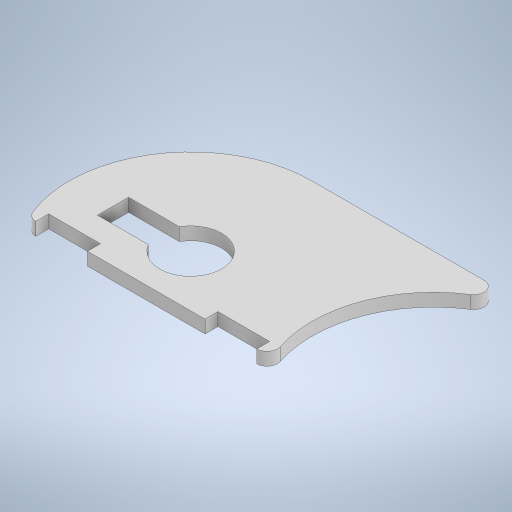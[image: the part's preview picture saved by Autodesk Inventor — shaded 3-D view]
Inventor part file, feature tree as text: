
AUTODESK INVENTOR PART (.ipt)
format: ipt  version: 2024.1 (Build 281209000, 209)  size: 267,264 bytes
history: native  units: mm
features: extrude x2, sketch x2, other x1, fillet x1
ambient origin geometry x8: Origin, YZ Plane, XZ Plane, XY Plane, X Axis, Y Axis, Z Axis, Center Point
bodies: Body1 (feature_tree)
feature tree (6):
  other  "ソリッド1"
  extrude  "押し出し1"  Depth=12.0mm
  fillet  "フィレット2"  Radius=15.0mm
  extrude  "押し出し2"  Depth=6.0mm
  sketch  "スケッチ1"
  sketch  "スケッチ2"
